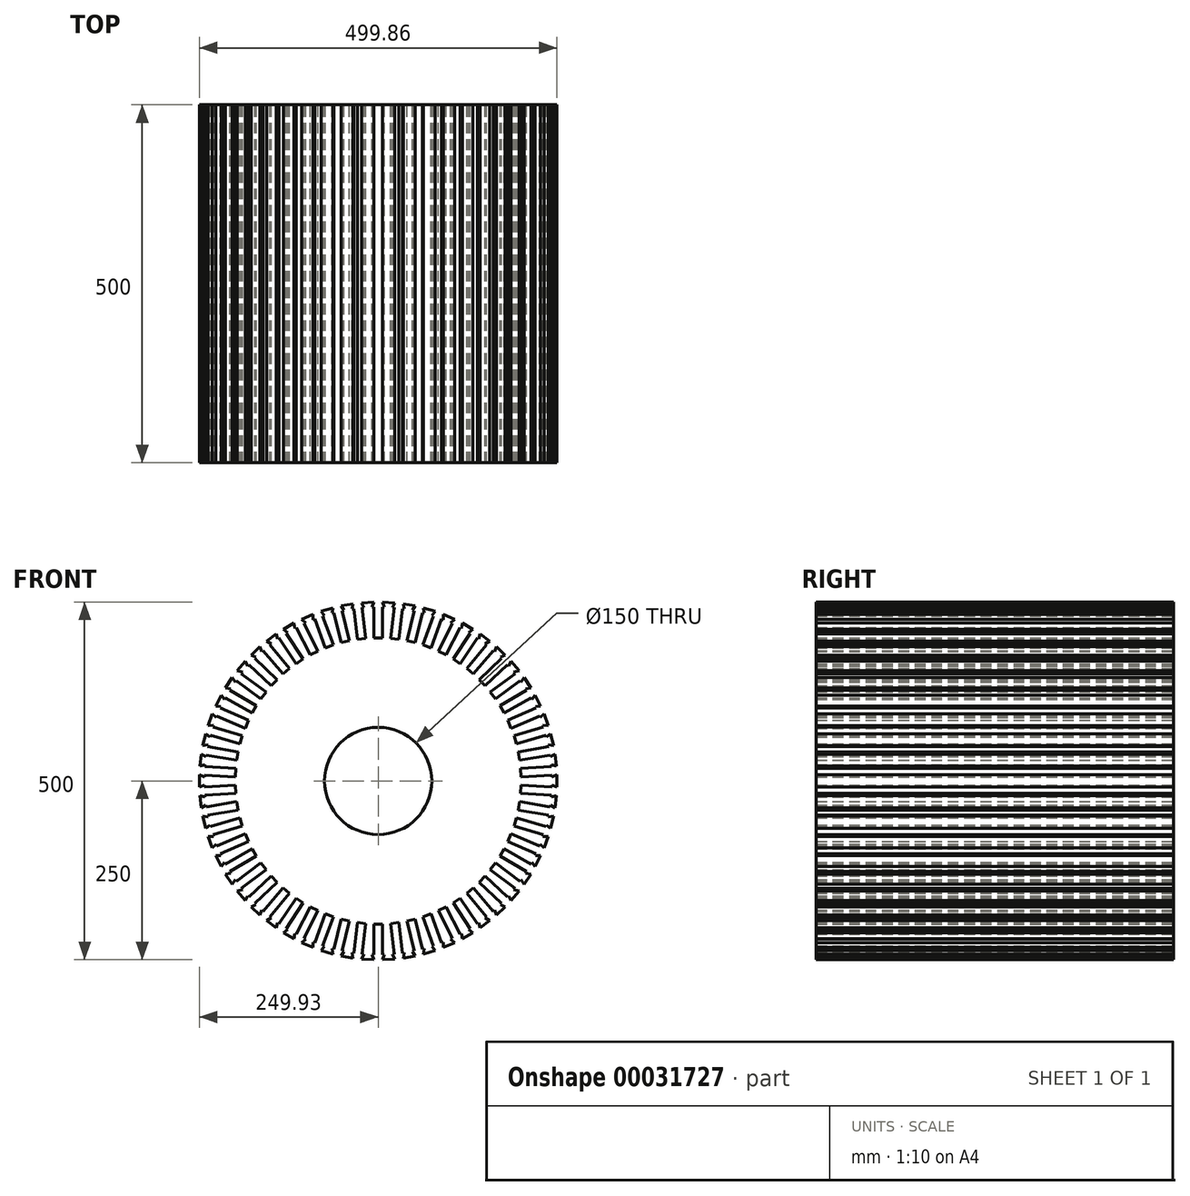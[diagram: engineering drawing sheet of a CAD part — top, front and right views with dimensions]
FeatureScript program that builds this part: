
annotation { "Feature Type Name" : "Feature", "Feature Type Description" : "" }
export const myFeature = defineFeature(function(context is Context, id is Id, definition is map)
    precondition{}
    {
        {
            var Q0;
            Q0=qCreatedBy(makeId("Front.planeOp"),FACE);
            var sketch = newSketch(context, id + "F0", { "sketchPlane" : qUnion([Q0])});
            skCircle(sketch, "E0", {"center": v(0, 0) * mm, "radius": 250 * mm, "construction": true});
            skCircle(sketch, "E1", {"center": v(0, 0) * mm, "radius": 75 * mm});
            skLineSegment(sketch, "E2", {"start": v(0, 0) * mm, "end": v(0, 250) * mm, "construction": true});
            skLineSegment(sketch, "E3.MirrorCS", {"start": v(6, 243) * mm, "end": v(6, 200) * mm});
            skPoint(sketch, "E4.orphan", {"position": v(6, 250) * mm});
            skLineSegment(sketch, "E5", {"start": v(-6, 243) * mm, "end": v(-6, 200) * mm});
            skLineSegment(sketch, "E6.MirrorCS", {"start": v(6, 200) * mm, "end": v(0, 200) * mm});
            skLineSegment(sketch, "E7", {"start": v(-6, 200) * mm, "end": v(0, 200) * mm});
            skLineSegment(sketch, "E8.MirrorCS", {"start": v(6, 250) * mm, "end": v(8.5, 243) * mm});
            skLineSegment(sketch, "E9.MirrorCS", {"start": v(6, 250) * mm, "end": v(0, 250) * mm, "construction": true});
            skLineSegment(sketch, "E10", {"start": v(-6, 250) * mm, "end": v(-8.5, 243) * mm});
            skLineSegment(sketch, "E11", {"start": v(-8.5, 243) * mm, "end": v(-6, 243) * mm});
            skLineSegment(sketch, "E12", {"start": v(0, 250) * mm, "end": v(0, -95.6) * mm, "construction": true});
            skLineSegment(sketch, "E13", {"start": v(-6, 250) * mm, "end": v(0, 250) * mm, "construction": true});
            skLineSegment(sketch, "E14.MirrorCS", {"start": v(8.5, 243) * mm, "end": v(6, 243) * mm});
            skLineSegment(sketch, "E15.1.0", {"start": v(-34.98, 247.61) * mm, "end": v(-29.02, 248.3) * mm, "construction": true});
            skLineSegment(sketch, "E15.1.1", {"start": v(-19.77, 242.34) * mm, "end": v(-22.25, 242.05) * mm});
            skLineSegment(sketch, "E15.1.4", {"start": v(-22.25, 242.05) * mm, "end": v(-17.26, 199.34) * mm});
            skLineSegment(sketch, "E15.1.5", {"start": v(-34.17, 240.66) * mm, "end": v(-29.18, 197.95) * mm});
            skLineSegment(sketch, "E15.1.6", {"start": v(-17.26, 199.34) * mm, "end": v(-23.22, 198.65) * mm});
            skLineSegment(sketch, "E15.1.9", {"start": v(-29.18, 197.95) * mm, "end": v(-23.22, 198.65) * mm});
            skPoint(sketch, "E15.1.15", {"position": v(-23.06, 249) * mm});
            skLineSegment(sketch, "E15.1.16", {"start": v(-34.98, 247.61) * mm, "end": v(-36.65, 240.37) * mm});
            skLineSegment(sketch, "E15.1.17", {"start": v(-23.06, 249) * mm, "end": v(-19.77, 242.34) * mm});
            skLineSegment(sketch, "E15.1.18", {"start": v(-23.06, 249) * mm, "end": v(-29.02, 248.3) * mm, "construction": true});
            skLineSegment(sketch, "E15.1.19", {"start": v(-36.65, 240.37) * mm, "end": v(-34.17, 240.66) * mm});
            skLineSegment(sketch, "E15.2.0", {"start": v(-63.5, 241.88) * mm, "end": v(-57.65, 243.26) * mm, "construction": true});
            skLineSegment(sketch, "E15.2.1", {"start": v(-47.77, 238.41) * mm, "end": v(-50.2, 237.83) * mm});
            skLineSegment(sketch, "E15.2.4", {"start": v(-50.2, 237.83) * mm, "end": v(-40.28, 196) * mm});
            skLineSegment(sketch, "E15.2.5", {"start": v(-61.88, 235.07) * mm, "end": v(-51.96, 193.23) * mm});
            skLineSegment(sketch, "E15.2.6", {"start": v(-40.28, 196) * mm, "end": v(-46.12, 194.6) * mm});
            skLineSegment(sketch, "E15.2.9", {"start": v(-51.96, 193.23) * mm, "end": v(-46.12, 194.6) * mm});
            skPoint(sketch, "E15.2.15", {"position": v(-51.82, 244.64) * mm});
            skLineSegment(sketch, "E15.2.16", {"start": v(-63.5, 241.88) * mm, "end": v(-64.31, 234.49) * mm});
            skLineSegment(sketch, "E15.2.17", {"start": v(-51.82, 244.64) * mm, "end": v(-47.77, 238.41) * mm});
            skLineSegment(sketch, "E15.2.18", {"start": v(-51.82, 244.64) * mm, "end": v(-57.65, 243.26) * mm, "construction": true});
            skLineSegment(sketch, "E15.2.19", {"start": v(-64.31, 234.49) * mm, "end": v(-61.88, 235.07) * mm});
            skLineSegment(sketch, "E15.3.0", {"start": v(-91.14, 232.87) * mm, "end": v(-85.5, 234.92) * mm, "construction": true});
            skLineSegment(sketch, "E15.3.1", {"start": v(-75.12, 231.25) * mm, "end": v(-77.47, 230.4) * mm});
            skLineSegment(sketch, "E15.3.4", {"start": v(-77.47, 230.4) * mm, "end": v(-62.77, 190) * mm});
            skLineSegment(sketch, "E15.3.5", {"start": v(-88.75, 226.3) * mm, "end": v(-74.04, 185.89) * mm});
            skLineSegment(sketch, "E15.3.6", {"start": v(-62.77, 190) * mm, "end": v(-68.4, 187.94) * mm});
            skLineSegment(sketch, "E15.3.9", {"start": v(-74.04, 185.89) * mm, "end": v(-68.4, 187.94) * mm});
            skPoint(sketch, "E15.3.15", {"position": v(-79.87, 236.98) * mm});
            skLineSegment(sketch, "E15.3.16", {"start": v(-91.14, 232.87) * mm, "end": v(-91.1, 225.44) * mm});
            skLineSegment(sketch, "E15.3.17", {"start": v(-79.87, 236.98) * mm, "end": v(-75.12, 231.25) * mm});
            skLineSegment(sketch, "E15.3.18", {"start": v(-79.87, 236.98) * mm, "end": v(-85.5, 234.92) * mm, "construction": true});
            skLineSegment(sketch, "E15.3.19", {"start": v(-91.1, 225.44) * mm, "end": v(-88.75, 226.3) * mm});
            skLineSegment(sketch, "E15.4.0", {"start": v(-117.56, 220.72) * mm, "end": v(-112.2, 223.4) * mm, "construction": true});
            skLineSegment(sketch, "E15.4.1", {"start": v(-101.46, 220.97) * mm, "end": v(-103.7, 219.85) * mm});
            skLineSegment(sketch, "E15.4.4", {"start": v(-103.7, 219.85) * mm, "end": v(-84.4, 181.42) * mm});
            skLineSegment(sketch, "E15.4.5", {"start": v(-114.42, 214.46) * mm, "end": v(-95.12, 176.03) * mm});
            skLineSegment(sketch, "E15.4.6", {"start": v(-84.4, 181.42) * mm, "end": v(-89.76, 178.73) * mm});
            skLineSegment(sketch, "E15.4.9", {"start": v(-95.12, 176.03) * mm, "end": v(-89.76, 178.73) * mm});
            skPoint(sketch, "E15.4.15", {"position": v(-106.84, 226.1) * mm});
            skLineSegment(sketch, "E15.4.16", {"start": v(-117.56, 220.72) * mm, "end": v(-116.65, 213.34) * mm});
            skLineSegment(sketch, "E15.4.17", {"start": v(-106.84, 226.1) * mm, "end": v(-101.46, 220.97) * mm});
            skLineSegment(sketch, "E15.4.18", {"start": v(-106.84, 226.1) * mm, "end": v(-112.2, 223.4) * mm, "construction": true});
            skLineSegment(sketch, "E15.4.19", {"start": v(-116.65, 213.34) * mm, "end": v(-114.42, 214.46) * mm});
            skLineSegment(sketch, "E15.5.0", {"start": v(-142.4, 205.57) * mm, "end": v(-137.38, 208.87) * mm, "construction": true});
            skLineSegment(sketch, "E15.5.1", {"start": v(-126.43, 207.7) * mm, "end": v(-128.52, 206.32) * mm});
            skLineSegment(sketch, "E15.5.4", {"start": v(-128.52, 206.32) * mm, "end": v(-104.89, 170.4) * mm});
            skLineSegment(sketch, "E15.5.5", {"start": v(-138.54, 199.73) * mm, "end": v(-114.91, 163.8) * mm});
            skLineSegment(sketch, "E15.5.6", {"start": v(-104.89, 170.4) * mm, "end": v(-109.9, 167.1) * mm});
            skLineSegment(sketch, "E15.5.9", {"start": v(-114.91, 163.8) * mm, "end": v(-109.9, 167.1) * mm});
            skPoint(sketch, "E15.5.15", {"position": v(-132.36, 212.17) * mm});
            skLineSegment(sketch, "E15.5.16", {"start": v(-142.4, 205.57) * mm, "end": v(-140.63, 198.35) * mm});
            skLineSegment(sketch, "E15.5.17", {"start": v(-132.36, 212.17) * mm, "end": v(-126.43, 207.7) * mm});
            skLineSegment(sketch, "E15.5.18", {"start": v(-132.36, 212.17) * mm, "end": v(-137.38, 208.87) * mm, "construction": true});
            skLineSegment(sketch, "E15.5.19", {"start": v(-140.63, 198.35) * mm, "end": v(-138.54, 199.73) * mm});
            skLineSegment(sketch, "E15.6.0", {"start": v(-165.3, 187.65) * mm, "end": v(-160.7, 191.51) * mm, "construction": true});
            skLineSegment(sketch, "E15.6.1", {"start": v(-149.69, 191.61) * mm, "end": v(-151.6, 190) * mm});
            skLineSegment(sketch, "E15.6.4", {"start": v(-151.6, 190) * mm, "end": v(-123.96, 157.07) * mm});
            skLineSegment(sketch, "E15.6.5", {"start": v(-160.8, 182.3) * mm, "end": v(-133.15, 149.35) * mm});
            skLineSegment(sketch, "E15.6.6", {"start": v(-123.96, 157.07) * mm, "end": v(-128.56, 153.2) * mm});
            skLineSegment(sketch, "E15.6.9", {"start": v(-133.15, 149.35) * mm, "end": v(-128.56, 153.2) * mm});
            skPoint(sketch, "E15.6.15", {"position": v(-156.1, 195.37) * mm});
            skLineSegment(sketch, "E15.6.16", {"start": v(-165.3, 187.65) * mm, "end": v(-162.7, 180.69) * mm});
            skLineSegment(sketch, "E15.6.17", {"start": v(-156.1, 195.37) * mm, "end": v(-149.69, 191.61) * mm});
            skLineSegment(sketch, "E15.6.18", {"start": v(-156.1, 195.37) * mm, "end": v(-160.7, 191.51) * mm, "construction": true});
            skLineSegment(sketch, "E15.6.19", {"start": v(-162.7, 180.69) * mm, "end": v(-160.8, 182.3) * mm});
            skLineSegment(sketch, "E15.7.0", {"start": v(-185.96, 167.2) * mm, "end": v(-181.84, 171.56) * mm, "construction": true});
            skLineSegment(sketch, "E15.7.1", {"start": v(-170.92, 172.94) * mm, "end": v(-172.63, 171.12) * mm});
            skLineSegment(sketch, "E15.7.4", {"start": v(-172.63, 171.12) * mm, "end": v(-141.36, 141.61) * mm});
            skLineSegment(sketch, "E15.7.5", {"start": v(-180.87, 162.4) * mm, "end": v(-149.6, 132.88) * mm});
            skLineSegment(sketch, "E15.7.6", {"start": v(-141.36, 141.61) * mm, "end": v(-145.47, 137.25) * mm});
            skLineSegment(sketch, "E15.7.9", {"start": v(-149.6, 132.88) * mm, "end": v(-145.47, 137.25) * mm});
            skPoint(sketch, "E15.7.15", {"position": v(-177.73, 175.92) * mm});
            skLineSegment(sketch, "E15.7.16", {"start": v(-185.96, 167.2) * mm, "end": v(-182.58, 160.57) * mm});
            skLineSegment(sketch, "E15.7.17", {"start": v(-177.73, 175.92) * mm, "end": v(-170.92, 172.94) * mm});
            skLineSegment(sketch, "E15.7.18", {"start": v(-177.73, 175.92) * mm, "end": v(-181.84, 171.56) * mm, "construction": true});
            skLineSegment(sketch, "E15.7.19", {"start": v(-182.58, 160.57) * mm, "end": v(-180.87, 162.4) * mm});
            skLineSegment(sketch, "E15.8.0", {"start": v(-204.11, 144.48) * mm, "end": v(-200.53, 149.29) * mm, "construction": true});
            skLineSegment(sketch, "E15.8.1", {"start": v(-189.84, 151.93) * mm, "end": v(-191.33, 149.92) * mm});
            skLineSegment(sketch, "E15.8.4", {"start": v(-191.33, 149.92) * mm, "end": v(-156.84, 124.24) * mm});
            skLineSegment(sketch, "E15.8.5", {"start": v(-198.5, 140.3) * mm, "end": v(-164, 114.62) * mm});
            skLineSegment(sketch, "E15.8.6", {"start": v(-156.84, 124.24) * mm, "end": v(-160.42, 119.43) * mm});
            skLineSegment(sketch, "E15.8.9", {"start": v(-164, 114.62) * mm, "end": v(-160.42, 119.43) * mm});
            skPoint(sketch, "E15.8.15", {"position": v(-196.95, 154.1) * mm});
            skLineSegment(sketch, "E15.8.16", {"start": v(-204.11, 144.48) * mm, "end": v(-200, 138.3) * mm});
            skLineSegment(sketch, "E15.8.17", {"start": v(-196.95, 154.1) * mm, "end": v(-189.84, 151.93) * mm});
            skLineSegment(sketch, "E15.8.18", {"start": v(-196.95, 154.1) * mm, "end": v(-200.53, 149.29) * mm, "construction": true});
            skLineSegment(sketch, "E15.8.19", {"start": v(-200, 138.3) * mm, "end": v(-198.5, 140.3) * mm});
            skLineSegment(sketch, "E15.9.0", {"start": v(-219.5, 119.8) * mm, "end": v(-216.5, 125) * mm, "construction": true});
            skLineSegment(sketch, "E15.9.1", {"start": v(-206.2, 128.86) * mm, "end": v(-207.44, 126.7) * mm});
            skLineSegment(sketch, "E15.9.4", {"start": v(-207.44, 126.7) * mm, "end": v(-170.2, 105.2) * mm});
            skLineSegment(sketch, "E15.9.5", {"start": v(-213.44, 116.3) * mm, "end": v(-176.2, 94.8) * mm});
            skLineSegment(sketch, "E15.9.6", {"start": v(-170.2, 105.2) * mm, "end": v(-173.2, 100) * mm});
            skLineSegment(sketch, "E15.9.9", {"start": v(-176.2, 94.8) * mm, "end": v(-173.2, 100) * mm});
            skPoint(sketch, "E15.9.15", {"position": v(-213.5, 130.2) * mm});
            skLineSegment(sketch, "E15.9.16", {"start": v(-219.5, 119.8) * mm, "end": v(-214.7, 114.14) * mm});
            skLineSegment(sketch, "E15.9.17", {"start": v(-213.5, 130.2) * mm, "end": v(-206.2, 128.86) * mm});
            skLineSegment(sketch, "E15.9.18", {"start": v(-213.5, 130.2) * mm, "end": v(-216.5, 125) * mm, "construction": true});
            skLineSegment(sketch, "E15.9.19", {"start": v(-214.7, 114.14) * mm, "end": v(-213.44, 116.3) * mm});
            skLineSegment(sketch, "E15.10.0", {"start": v(-231.93, 93.51) * mm, "end": v(-229.55, 99.02) * mm, "construction": true});
            skLineSegment(sketch, "E15.10.1", {"start": v(-219.76, 104.05) * mm, "end": v(-220.75, 101.76) * mm});
            skLineSegment(sketch, "E15.10.4", {"start": v(-220.75, 101.76) * mm, "end": v(-181.27, 84.73) * mm});
            skLineSegment(sketch, "E15.10.5", {"start": v(-225.5, 90.74) * mm, "end": v(-186.02, 73.7) * mm});
            skLineSegment(sketch, "E15.10.6", {"start": v(-181.27, 84.73) * mm, "end": v(-183.64, 79.22) * mm});
            skLineSegment(sketch, "E15.10.9", {"start": v(-186.02, 73.7) * mm, "end": v(-183.64, 79.22) * mm});
            skPoint(sketch, "E15.10.15", {"position": v(-227.18, 104.53) * mm});
            skLineSegment(sketch, "E15.10.16", {"start": v(-231.93, 93.51) * mm, "end": v(-226.5, 88.44) * mm});
            skLineSegment(sketch, "E15.10.17", {"start": v(-227.18, 104.53) * mm, "end": v(-219.76, 104.05) * mm});
            skLineSegment(sketch, "E15.10.18", {"start": v(-227.18, 104.53) * mm, "end": v(-229.55, 99.02) * mm, "construction": true});
            skLineSegment(sketch, "E15.10.19", {"start": v(-226.5, 88.44) * mm, "end": v(-225.5, 90.74) * mm});
            skLineSegment(sketch, "E15.11.0", {"start": v(-241.22, 65.95) * mm, "end": v(-239.5, 71.7) * mm, "construction": true});
            skLineSegment(sketch, "E15.11.1", {"start": v(-230.35, 77.84) * mm, "end": v(-231.07, 75.44) * mm});
            skLineSegment(sketch, "E15.11.4", {"start": v(-231.07, 75.44) * mm, "end": v(-189.88, 63.1) * mm});
            skLineSegment(sketch, "E15.11.5", {"start": v(-234.51, 63.95) * mm, "end": v(-193.32, 51.61) * mm});
            skLineSegment(sketch, "E15.11.6", {"start": v(-189.88, 63.1) * mm, "end": v(-191.6, 57.36) * mm});
            skLineSegment(sketch, "E15.11.9", {"start": v(-193.32, 51.61) * mm, "end": v(-191.6, 57.36) * mm});
            skPoint(sketch, "E15.11.15", {"position": v(-237.78, 77.45) * mm});
            skLineSegment(sketch, "E15.11.16", {"start": v(-241.22, 65.95) * mm, "end": v(-235.23, 61.55) * mm});
            skLineSegment(sketch, "E15.11.17", {"start": v(-237.78, 77.45) * mm, "end": v(-230.35, 77.84) * mm});
            skLineSegment(sketch, "E15.11.18", {"start": v(-237.78, 77.45) * mm, "end": v(-239.5, 71.7) * mm, "construction": true});
            skLineSegment(sketch, "E15.11.19", {"start": v(-235.23, 61.55) * mm, "end": v(-234.51, 63.95) * mm});
            skLineSegment(sketch, "E15.12.0", {"start": v(-247.24, 37.5) * mm, "end": v(-246.2, 43.41) * mm, "construction": true});
            skLineSegment(sketch, "E15.12.1", {"start": v(-237.83, 50.57) * mm, "end": v(-238.27, 48.1) * mm});
            skLineSegment(sketch, "E15.12.4", {"start": v(-238.27, 48.1) * mm, "end": v(-195.92, 40.64) * mm});
            skLineSegment(sketch, "E15.12.5", {"start": v(-240.35, 36.29) * mm, "end": v(-198, 28.82) * mm});
            skLineSegment(sketch, "E15.12.6", {"start": v(-195.92, 40.64) * mm, "end": v(-196.96, 34.73) * mm});
            skLineSegment(sketch, "E15.12.9", {"start": v(-198, 28.82) * mm, "end": v(-196.96, 34.73) * mm});
            skPoint(sketch, "E15.12.15", {"position": v(-245.16, 49.32) * mm});
            skLineSegment(sketch, "E15.12.16", {"start": v(-247.24, 37.5) * mm, "end": v(-240.78, 33.83) * mm});
            skLineSegment(sketch, "E15.12.17", {"start": v(-245.16, 49.32) * mm, "end": v(-237.83, 50.57) * mm});
            skLineSegment(sketch, "E15.12.18", {"start": v(-245.16, 49.32) * mm, "end": v(-246.2, 43.41) * mm, "construction": true});
            skLineSegment(sketch, "E15.12.19", {"start": v(-240.78, 33.83) * mm, "end": v(-240.35, 36.29) * mm});
            skLineSegment(sketch, "E15.13.0", {"start": v(-249.93, 8.55) * mm, "end": v(-249.58, 14.54) * mm, "construction": true});
            skLineSegment(sketch, "E15.13.1", {"start": v(-242.1, 22.61) * mm, "end": v(-242.24, 20.12) * mm});
            skLineSegment(sketch, "E15.13.4", {"start": v(-242.24, 20.12) * mm, "end": v(-199.31, 17.62) * mm});
            skLineSegment(sketch, "E15.13.5", {"start": v(-242.94, 8.14) * mm, "end": v(-200.01, 5.64) * mm});
            skLineSegment(sketch, "E15.13.6", {"start": v(-199.31, 17.62) * mm, "end": v(-199.66, 11.63) * mm});
            skLineSegment(sketch, "E15.13.9", {"start": v(-200.01, 5.64) * mm, "end": v(-199.66, 11.63) * mm});
            skPoint(sketch, "E15.13.15", {"position": v(-249.23, 20.53) * mm});
            skLineSegment(sketch, "E15.13.16", {"start": v(-249.93, 8.55) * mm, "end": v(-243.08, 5.64) * mm});
            skLineSegment(sketch, "E15.13.17", {"start": v(-249.23, 20.53) * mm, "end": v(-242.1, 22.61) * mm});
            skLineSegment(sketch, "E15.13.18", {"start": v(-249.23, 20.53) * mm, "end": v(-249.58, 14.54) * mm, "construction": true});
            skLineSegment(sketch, "E15.13.19", {"start": v(-243.08, 5.64) * mm, "end": v(-242.94, 8.14) * mm});
            skLineSegment(sketch, "E15.14.0", {"start": v(-249.23, -20.53) * mm, "end": v(-249.58, -14.54) * mm, "construction": true});
            skLineSegment(sketch, "E15.14.1", {"start": v(-243.08, -5.64) * mm, "end": v(-242.94, -8.14) * mm});
            skLineSegment(sketch, "E15.14.4", {"start": v(-242.94, -8.14) * mm, "end": v(-200.01, -5.64) * mm});
            skLineSegment(sketch, "E15.14.5", {"start": v(-242.24, -20.12) * mm, "end": v(-199.31, -17.62) * mm});
            skLineSegment(sketch, "E15.14.6", {"start": v(-200.01, -5.64) * mm, "end": v(-199.66, -11.63) * mm});
            skLineSegment(sketch, "E15.14.9", {"start": v(-199.31, -17.62) * mm, "end": v(-199.66, -11.63) * mm});
            skPoint(sketch, "E15.14.15", {"position": v(-249.93, -8.55) * mm});
            skLineSegment(sketch, "E15.14.16", {"start": v(-249.23, -20.53) * mm, "end": v(-242.1, -22.61) * mm});
            skLineSegment(sketch, "E15.14.17", {"start": v(-249.93, -8.55) * mm, "end": v(-243.08, -5.64) * mm});
            skLineSegment(sketch, "E15.14.18", {"start": v(-249.93, -8.55) * mm, "end": v(-249.58, -14.54) * mm, "construction": true});
            skLineSegment(sketch, "E15.14.19", {"start": v(-242.1, -22.61) * mm, "end": v(-242.24, -20.12) * mm});
            skLineSegment(sketch, "E15.15.0", {"start": v(-245.16, -49.32) * mm, "end": v(-246.2, -43.41) * mm, "construction": true});
            skLineSegment(sketch, "E15.15.1", {"start": v(-240.78, -33.83) * mm, "end": v(-240.35, -36.29) * mm});
            skLineSegment(sketch, "E15.15.4", {"start": v(-240.35, -36.29) * mm, "end": v(-198, -28.82) * mm});
            skLineSegment(sketch, "E15.15.5", {"start": v(-238.27, -48.1) * mm, "end": v(-195.92, -40.64) * mm});
            skLineSegment(sketch, "E15.15.6", {"start": v(-198, -28.82) * mm, "end": v(-196.96, -34.73) * mm});
            skLineSegment(sketch, "E15.15.9", {"start": v(-195.92, -40.64) * mm, "end": v(-196.96, -34.73) * mm});
            skPoint(sketch, "E15.15.15", {"position": v(-247.24, -37.5) * mm});
            skLineSegment(sketch, "E15.15.16", {"start": v(-245.16, -49.32) * mm, "end": v(-237.83, -50.57) * mm});
            skLineSegment(sketch, "E15.15.17", {"start": v(-247.24, -37.5) * mm, "end": v(-240.78, -33.83) * mm});
            skLineSegment(sketch, "E15.15.18", {"start": v(-247.24, -37.5) * mm, "end": v(-246.2, -43.41) * mm, "construction": true});
            skLineSegment(sketch, "E15.15.19", {"start": v(-237.83, -50.57) * mm, "end": v(-238.27, -48.1) * mm});
            skLineSegment(sketch, "E15.16.0", {"start": v(-237.78, -77.45) * mm, "end": v(-239.5, -71.7) * mm, "construction": true});
            skLineSegment(sketch, "E15.16.1", {"start": v(-235.23, -61.55) * mm, "end": v(-234.51, -63.95) * mm});
            skLineSegment(sketch, "E15.16.4", {"start": v(-234.51, -63.95) * mm, "end": v(-193.32, -51.61) * mm});
            skLineSegment(sketch, "E15.16.5", {"start": v(-231.07, -75.44) * mm, "end": v(-189.88, -63.1) * mm});
            skLineSegment(sketch, "E15.16.6", {"start": v(-193.32, -51.61) * mm, "end": v(-191.6, -57.36) * mm});
            skLineSegment(sketch, "E15.16.9", {"start": v(-189.88, -63.1) * mm, "end": v(-191.6, -57.36) * mm});
            skPoint(sketch, "E15.16.15", {"position": v(-241.22, -65.95) * mm});
            skLineSegment(sketch, "E15.16.16", {"start": v(-237.78, -77.45) * mm, "end": v(-230.35, -77.84) * mm});
            skLineSegment(sketch, "E15.16.17", {"start": v(-241.22, -65.95) * mm, "end": v(-235.23, -61.55) * mm});
            skLineSegment(sketch, "E15.16.18", {"start": v(-241.22, -65.95) * mm, "end": v(-239.5, -71.7) * mm, "construction": true});
            skLineSegment(sketch, "E15.16.19", {"start": v(-230.35, -77.84) * mm, "end": v(-231.07, -75.44) * mm});
            skLineSegment(sketch, "E15.17.0", {"start": v(-227.18, -104.53) * mm, "end": v(-229.55, -99.02) * mm, "construction": true});
            skLineSegment(sketch, "E15.17.1", {"start": v(-226.5, -88.44) * mm, "end": v(-225.5, -90.74) * mm});
            skLineSegment(sketch, "E15.17.4", {"start": v(-225.5, -90.74) * mm, "end": v(-186.02, -73.7) * mm});
            skLineSegment(sketch, "E15.17.5", {"start": v(-220.75, -101.76) * mm, "end": v(-181.27, -84.73) * mm});
            skLineSegment(sketch, "E15.17.6", {"start": v(-186.02, -73.7) * mm, "end": v(-183.64, -79.22) * mm});
            skLineSegment(sketch, "E15.17.9", {"start": v(-181.27, -84.73) * mm, "end": v(-183.64, -79.22) * mm});
            skPoint(sketch, "E15.17.15", {"position": v(-231.93, -93.51) * mm});
            skLineSegment(sketch, "E15.17.16", {"start": v(-227.18, -104.53) * mm, "end": v(-219.76, -104.05) * mm});
            skLineSegment(sketch, "E15.17.17", {"start": v(-231.93, -93.51) * mm, "end": v(-226.5, -88.44) * mm});
            skLineSegment(sketch, "E15.17.18", {"start": v(-231.93, -93.51) * mm, "end": v(-229.55, -99.02) * mm, "construction": true});
            skLineSegment(sketch, "E15.17.19", {"start": v(-219.76, -104.05) * mm, "end": v(-220.75, -101.76) * mm});
            skLineSegment(sketch, "E15.18.0", {"start": v(-213.5, -130.2) * mm, "end": v(-216.5, -125) * mm, "construction": true});
            skLineSegment(sketch, "E15.18.1", {"start": v(-214.7, -114.14) * mm, "end": v(-213.44, -116.3) * mm});
            skLineSegment(sketch, "E15.18.4", {"start": v(-213.44, -116.3) * mm, "end": v(-176.2, -94.8) * mm});
            skLineSegment(sketch, "E15.18.5", {"start": v(-207.44, -126.7) * mm, "end": v(-170.2, -105.2) * mm});
            skLineSegment(sketch, "E15.18.6", {"start": v(-176.2, -94.8) * mm, "end": v(-173.2, -100) * mm});
            skLineSegment(sketch, "E15.18.9", {"start": v(-170.2, -105.2) * mm, "end": v(-173.2, -100) * mm});
            skPoint(sketch, "E15.18.15", {"position": v(-219.5, -119.8) * mm});
            skLineSegment(sketch, "E15.18.16", {"start": v(-213.5, -130.2) * mm, "end": v(-206.2, -128.86) * mm});
            skLineSegment(sketch, "E15.18.17", {"start": v(-219.5, -119.8) * mm, "end": v(-214.7, -114.14) * mm});
            skLineSegment(sketch, "E15.18.18", {"start": v(-219.5, -119.8) * mm, "end": v(-216.5, -125) * mm, "construction": true});
            skLineSegment(sketch, "E15.18.19", {"start": v(-206.2, -128.86) * mm, "end": v(-207.44, -126.7) * mm});
            skLineSegment(sketch, "E15.19.0", {"start": v(-196.95, -154.1) * mm, "end": v(-200.53, -149.29) * mm, "construction": true});
            skLineSegment(sketch, "E15.19.1", {"start": v(-200, -138.3) * mm, "end": v(-198.5, -140.3) * mm});
            skLineSegment(sketch, "E15.19.4", {"start": v(-198.5, -140.3) * mm, "end": v(-164, -114.62) * mm});
            skLineSegment(sketch, "E15.19.5", {"start": v(-191.33, -149.92) * mm, "end": v(-156.84, -124.24) * mm});
            skLineSegment(sketch, "E15.19.6", {"start": v(-164, -114.62) * mm, "end": v(-160.42, -119.43) * mm});
            skLineSegment(sketch, "E15.19.9", {"start": v(-156.84, -124.24) * mm, "end": v(-160.42, -119.43) * mm});
            skPoint(sketch, "E15.19.15", {"position": v(-204.11, -144.48) * mm});
            skLineSegment(sketch, "E15.19.16", {"start": v(-196.95, -154.1) * mm, "end": v(-189.84, -151.93) * mm});
            skLineSegment(sketch, "E15.19.17", {"start": v(-204.11, -144.48) * mm, "end": v(-200, -138.3) * mm});
            skLineSegment(sketch, "E15.19.18", {"start": v(-204.11, -144.48) * mm, "end": v(-200.53, -149.29) * mm, "construction": true});
            skLineSegment(sketch, "E15.19.19", {"start": v(-189.84, -151.93) * mm, "end": v(-191.33, -149.92) * mm});
            skLineSegment(sketch, "E15.20.0", {"start": v(-177.73, -175.92) * mm, "end": v(-181.84, -171.56) * mm, "construction": true});
            skLineSegment(sketch, "E15.20.1", {"start": v(-182.58, -160.57) * mm, "end": v(-180.87, -162.4) * mm});
            skLineSegment(sketch, "E15.20.4", {"start": v(-180.87, -162.4) * mm, "end": v(-149.6, -132.88) * mm});
            skLineSegment(sketch, "E15.20.5", {"start": v(-172.63, -171.12) * mm, "end": v(-141.36, -141.61) * mm});
            skLineSegment(sketch, "E15.20.6", {"start": v(-149.6, -132.88) * mm, "end": v(-145.47, -137.25) * mm});
            skLineSegment(sketch, "E15.20.9", {"start": v(-141.36, -141.61) * mm, "end": v(-145.47, -137.25) * mm});
            skPoint(sketch, "E15.20.15", {"position": v(-185.96, -167.2) * mm});
            skLineSegment(sketch, "E15.20.16", {"start": v(-177.73, -175.92) * mm, "end": v(-170.92, -172.94) * mm});
            skLineSegment(sketch, "E15.20.17", {"start": v(-185.96, -167.2) * mm, "end": v(-182.58, -160.57) * mm});
            skLineSegment(sketch, "E15.20.18", {"start": v(-185.96, -167.2) * mm, "end": v(-181.84, -171.56) * mm, "construction": true});
            skLineSegment(sketch, "E15.20.19", {"start": v(-170.92, -172.94) * mm, "end": v(-172.63, -171.12) * mm});
            skLineSegment(sketch, "E15.21.0", {"start": v(-156.1, -195.37) * mm, "end": v(-160.7, -191.51) * mm, "construction": true});
            skLineSegment(sketch, "E15.21.1", {"start": v(-162.7, -180.69) * mm, "end": v(-160.8, -182.3) * mm});
            skLineSegment(sketch, "E15.21.4", {"start": v(-160.8, -182.3) * mm, "end": v(-133.15, -149.35) * mm});
            skLineSegment(sketch, "E15.21.5", {"start": v(-151.6, -190) * mm, "end": v(-123.96, -157.07) * mm});
            skLineSegment(sketch, "E15.21.6", {"start": v(-133.15, -149.35) * mm, "end": v(-128.56, -153.2) * mm});
            skLineSegment(sketch, "E15.21.9", {"start": v(-123.96, -157.07) * mm, "end": v(-128.56, -153.2) * mm});
            skPoint(sketch, "E15.21.15", {"position": v(-165.3, -187.65) * mm});
            skLineSegment(sketch, "E15.21.16", {"start": v(-156.1, -195.37) * mm, "end": v(-149.69, -191.61) * mm});
            skLineSegment(sketch, "E15.21.17", {"start": v(-165.3, -187.65) * mm, "end": v(-162.7, -180.69) * mm});
            skLineSegment(sketch, "E15.21.18", {"start": v(-165.3, -187.65) * mm, "end": v(-160.7, -191.51) * mm, "construction": true});
            skLineSegment(sketch, "E15.21.19", {"start": v(-149.69, -191.61) * mm, "end": v(-151.6, -190) * mm});
            skLineSegment(sketch, "E15.22.0", {"start": v(-132.36, -212.17) * mm, "end": v(-137.38, -208.87) * mm, "construction": true});
            skLineSegment(sketch, "E15.22.1", {"start": v(-140.63, -198.35) * mm, "end": v(-138.54, -199.73) * mm});
            skLineSegment(sketch, "E15.22.4", {"start": v(-138.54, -199.73) * mm, "end": v(-114.91, -163.8) * mm});
            skLineSegment(sketch, "E15.22.5", {"start": v(-128.52, -206.32) * mm, "end": v(-104.89, -170.4) * mm});
            skLineSegment(sketch, "E15.22.6", {"start": v(-114.91, -163.8) * mm, "end": v(-109.9, -167.1) * mm});
            skLineSegment(sketch, "E15.22.9", {"start": v(-104.89, -170.4) * mm, "end": v(-109.9, -167.1) * mm});
            skPoint(sketch, "E15.22.15", {"position": v(-142.4, -205.57) * mm});
            skLineSegment(sketch, "E15.22.16", {"start": v(-132.36, -212.17) * mm, "end": v(-126.43, -207.7) * mm});
            skLineSegment(sketch, "E15.22.17", {"start": v(-142.4, -205.57) * mm, "end": v(-140.63, -198.35) * mm});
            skLineSegment(sketch, "E15.22.18", {"start": v(-142.4, -205.57) * mm, "end": v(-137.38, -208.87) * mm, "construction": true});
            skLineSegment(sketch, "E15.22.19", {"start": v(-126.43, -207.7) * mm, "end": v(-128.52, -206.32) * mm});
            skLineSegment(sketch, "E15.23.0", {"start": v(-106.84, -226.1) * mm, "end": v(-112.2, -223.4) * mm, "construction": true});
            skLineSegment(sketch, "E15.23.1", {"start": v(-116.65, -213.34) * mm, "end": v(-114.42, -214.46) * mm});
            skLineSegment(sketch, "E15.23.4", {"start": v(-114.42, -214.46) * mm, "end": v(-95.12, -176.03) * mm});
            skLineSegment(sketch, "E15.23.5", {"start": v(-103.7, -219.85) * mm, "end": v(-84.4, -181.42) * mm});
            skLineSegment(sketch, "E15.23.6", {"start": v(-95.12, -176.03) * mm, "end": v(-89.76, -178.73) * mm});
            skLineSegment(sketch, "E15.23.9", {"start": v(-84.4, -181.42) * mm, "end": v(-89.76, -178.73) * mm});
            skPoint(sketch, "E15.23.15", {"position": v(-117.56, -220.72) * mm});
            skLineSegment(sketch, "E15.23.16", {"start": v(-106.84, -226.1) * mm, "end": v(-101.46, -220.97) * mm});
            skLineSegment(sketch, "E15.23.17", {"start": v(-117.56, -220.72) * mm, "end": v(-116.65, -213.34) * mm});
            skLineSegment(sketch, "E15.23.18", {"start": v(-117.56, -220.72) * mm, "end": v(-112.2, -223.4) * mm, "construction": true});
            skLineSegment(sketch, "E15.23.19", {"start": v(-101.46, -220.97) * mm, "end": v(-103.7, -219.85) * mm});
            skLineSegment(sketch, "E15.24.0", {"start": v(-79.87, -236.98) * mm, "end": v(-85.5, -234.92) * mm, "construction": true});
            skLineSegment(sketch, "E15.24.1", {"start": v(-91.1, -225.44) * mm, "end": v(-88.75, -226.3) * mm});
            skLineSegment(sketch, "E15.24.4", {"start": v(-88.75, -226.3) * mm, "end": v(-74.04, -185.89) * mm});
            skLineSegment(sketch, "E15.24.5", {"start": v(-77.47, -230.4) * mm, "end": v(-62.77, -190) * mm});
            skLineSegment(sketch, "E15.24.6", {"start": v(-74.04, -185.89) * mm, "end": v(-68.4, -187.94) * mm});
            skLineSegment(sketch, "E15.24.9", {"start": v(-62.77, -190) * mm, "end": v(-68.4, -187.94) * mm});
            skPoint(sketch, "E15.24.15", {"position": v(-91.14, -232.87) * mm});
            skLineSegment(sketch, "E15.24.16", {"start": v(-79.87, -236.98) * mm, "end": v(-75.12, -231.25) * mm});
            skLineSegment(sketch, "E15.24.17", {"start": v(-91.14, -232.87) * mm, "end": v(-91.1, -225.44) * mm});
            skLineSegment(sketch, "E15.24.18", {"start": v(-91.14, -232.87) * mm, "end": v(-85.5, -234.92) * mm, "construction": true});
            skLineSegment(sketch, "E15.24.19", {"start": v(-75.12, -231.25) * mm, "end": v(-77.47, -230.4) * mm});
            skLineSegment(sketch, "E15.25.0", {"start": v(-51.82, -244.64) * mm, "end": v(-57.65, -243.26) * mm, "construction": true});
            skLineSegment(sketch, "E15.25.1", {"start": v(-64.31, -234.49) * mm, "end": v(-61.88, -235.07) * mm});
            skLineSegment(sketch, "E15.25.4", {"start": v(-61.88, -235.07) * mm, "end": v(-51.96, -193.23) * mm});
            skLineSegment(sketch, "E15.25.5", {"start": v(-50.2, -237.83) * mm, "end": v(-40.28, -196) * mm});
            skLineSegment(sketch, "E15.25.6", {"start": v(-51.96, -193.23) * mm, "end": v(-46.12, -194.6) * mm});
            skLineSegment(sketch, "E15.25.9", {"start": v(-40.28, -196) * mm, "end": v(-46.12, -194.6) * mm});
            skPoint(sketch, "E15.25.15", {"position": v(-63.5, -241.88) * mm});
            skLineSegment(sketch, "E15.25.16", {"start": v(-51.82, -244.64) * mm, "end": v(-47.77, -238.41) * mm});
            skLineSegment(sketch, "E15.25.17", {"start": v(-63.5, -241.88) * mm, "end": v(-64.31, -234.49) * mm});
            skLineSegment(sketch, "E15.25.18", {"start": v(-63.5, -241.88) * mm, "end": v(-57.65, -243.26) * mm, "construction": true});
            skLineSegment(sketch, "E15.25.19", {"start": v(-47.77, -238.41) * mm, "end": v(-50.2, -237.83) * mm});
            skLineSegment(sketch, "E15.26.0", {"start": v(-23.06, -249) * mm, "end": v(-29.02, -248.3) * mm, "construction": true});
            skLineSegment(sketch, "E15.26.1", {"start": v(-36.65, -240.37) * mm, "end": v(-34.17, -240.66) * mm});
            skLineSegment(sketch, "E15.26.4", {"start": v(-34.17, -240.66) * mm, "end": v(-29.18, -197.95) * mm});
            skLineSegment(sketch, "E15.26.5", {"start": v(-22.25, -242.05) * mm, "end": v(-17.26, -199.34) * mm});
            skLineSegment(sketch, "E15.26.6", {"start": v(-29.18, -197.95) * mm, "end": v(-23.22, -198.65) * mm});
            skLineSegment(sketch, "E15.26.9", {"start": v(-17.26, -199.34) * mm, "end": v(-23.22, -198.65) * mm});
            skPoint(sketch, "E15.26.15", {"position": v(-34.98, -247.61) * mm});
            skLineSegment(sketch, "E15.26.16", {"start": v(-23.06, -249) * mm, "end": v(-19.77, -242.34) * mm});
            skLineSegment(sketch, "E15.26.17", {"start": v(-34.98, -247.61) * mm, "end": v(-36.65, -240.37) * mm});
            skLineSegment(sketch, "E15.26.18", {"start": v(-34.98, -247.61) * mm, "end": v(-29.02, -248.3) * mm, "construction": true});
            skLineSegment(sketch, "E15.26.19", {"start": v(-19.77, -242.34) * mm, "end": v(-22.25, -242.05) * mm});
            skLineSegment(sketch, "E15.27.0", {"start": v(6, -250) * mm, "end": v(0, -250) * mm, "construction": true});
            skLineSegment(sketch, "E15.27.1", {"start": v(-8.5, -243) * mm, "end": v(-6, -243) * mm});
            skLineSegment(sketch, "E15.27.4", {"start": v(-6, -243) * mm, "end": v(-6, -200) * mm});
            skLineSegment(sketch, "E15.27.5", {"start": v(6, -243) * mm, "end": v(6, -200) * mm});
            skLineSegment(sketch, "E15.27.6", {"start": v(-6, -200) * mm, "end": v(0, -200) * mm});
            skLineSegment(sketch, "E15.27.9", {"start": v(6, -200) * mm, "end": v(0, -200) * mm});
            skPoint(sketch, "E15.27.15", {"position": v(-6, -250) * mm});
            skLineSegment(sketch, "E15.27.16", {"start": v(6, -250) * mm, "end": v(8.5, -243) * mm});
            skLineSegment(sketch, "E15.27.17", {"start": v(-6, -250) * mm, "end": v(-8.5, -243) * mm});
            skLineSegment(sketch, "E15.27.18", {"start": v(-6, -250) * mm, "end": v(0, -250) * mm, "construction": true});
            skLineSegment(sketch, "E15.27.19", {"start": v(8.5, -243) * mm, "end": v(6, -243) * mm});
            skLineSegment(sketch, "E15.28.0", {"start": v(34.98, -247.61) * mm, "end": v(29.02, -248.3) * mm, "construction": true});
            skLineSegment(sketch, "E15.28.1", {"start": v(19.77, -242.34) * mm, "end": v(22.25, -242.05) * mm});
            skLineSegment(sketch, "E15.28.4", {"start": v(22.25, -242.05) * mm, "end": v(17.26, -199.34) * mm});
            skLineSegment(sketch, "E15.28.5", {"start": v(34.17, -240.66) * mm, "end": v(29.18, -197.95) * mm});
            skLineSegment(sketch, "E15.28.6", {"start": v(17.26, -199.34) * mm, "end": v(23.22, -198.65) * mm});
            skLineSegment(sketch, "E15.28.9", {"start": v(29.18, -197.95) * mm, "end": v(23.22, -198.65) * mm});
            skPoint(sketch, "E15.28.15", {"position": v(23.06, -249) * mm});
            skLineSegment(sketch, "E15.28.16", {"start": v(34.98, -247.61) * mm, "end": v(36.65, -240.37) * mm});
            skLineSegment(sketch, "E15.28.17", {"start": v(23.06, -249) * mm, "end": v(19.77, -242.34) * mm});
            skLineSegment(sketch, "E15.28.18", {"start": v(23.06, -249) * mm, "end": v(29.02, -248.3) * mm, "construction": true});
            skLineSegment(sketch, "E15.28.19", {"start": v(36.65, -240.37) * mm, "end": v(34.17, -240.66) * mm});
            skLineSegment(sketch, "E15.29.0", {"start": v(63.5, -241.88) * mm, "end": v(57.65, -243.26) * mm, "construction": true});
            skLineSegment(sketch, "E15.29.1", {"start": v(47.77, -238.41) * mm, "end": v(50.2, -237.83) * mm});
            skLineSegment(sketch, "E15.29.4", {"start": v(50.2, -237.83) * mm, "end": v(40.28, -196) * mm});
            skLineSegment(sketch, "E15.29.5", {"start": v(61.88, -235.07) * mm, "end": v(51.96, -193.23) * mm});
            skLineSegment(sketch, "E15.29.6", {"start": v(40.28, -196) * mm, "end": v(46.12, -194.6) * mm});
            skLineSegment(sketch, "E15.29.9", {"start": v(51.96, -193.23) * mm, "end": v(46.12, -194.6) * mm});
            skPoint(sketch, "E15.29.15", {"position": v(51.82, -244.64) * mm});
            skLineSegment(sketch, "E15.29.16", {"start": v(63.5, -241.88) * mm, "end": v(64.31, -234.49) * mm});
            skLineSegment(sketch, "E15.29.17", {"start": v(51.82, -244.64) * mm, "end": v(47.77, -238.41) * mm});
            skLineSegment(sketch, "E15.29.18", {"start": v(51.82, -244.64) * mm, "end": v(57.65, -243.26) * mm, "construction": true});
            skLineSegment(sketch, "E15.29.19", {"start": v(64.31, -234.49) * mm, "end": v(61.88, -235.07) * mm});
            skLineSegment(sketch, "E15.30.0", {"start": v(91.14, -232.87) * mm, "end": v(85.5, -234.92) * mm, "construction": true});
            skLineSegment(sketch, "E15.30.1", {"start": v(75.12, -231.25) * mm, "end": v(77.47, -230.4) * mm});
            skLineSegment(sketch, "E15.30.4", {"start": v(77.47, -230.4) * mm, "end": v(62.77, -190) * mm});
            skLineSegment(sketch, "E15.30.5", {"start": v(88.75, -226.3) * mm, "end": v(74.04, -185.89) * mm});
            skLineSegment(sketch, "E15.30.6", {"start": v(62.77, -190) * mm, "end": v(68.4, -187.94) * mm});
            skLineSegment(sketch, "E15.30.9", {"start": v(74.04, -185.89) * mm, "end": v(68.4, -187.94) * mm});
            skPoint(sketch, "E15.30.15", {"position": v(79.87, -236.98) * mm});
            skLineSegment(sketch, "E15.30.16", {"start": v(91.14, -232.87) * mm, "end": v(91.1, -225.44) * mm});
            skLineSegment(sketch, "E15.30.17", {"start": v(79.87, -236.98) * mm, "end": v(75.12, -231.25) * mm});
            skLineSegment(sketch, "E15.30.18", {"start": v(79.87, -236.98) * mm, "end": v(85.5, -234.92) * mm, "construction": true});
            skLineSegment(sketch, "E15.30.19", {"start": v(91.1, -225.44) * mm, "end": v(88.75, -226.3) * mm});
            skLineSegment(sketch, "E15.31.0", {"start": v(117.56, -220.72) * mm, "end": v(112.2, -223.4) * mm, "construction": true});
            skLineSegment(sketch, "E15.31.1", {"start": v(101.46, -220.97) * mm, "end": v(103.7, -219.85) * mm});
            skLineSegment(sketch, "E15.31.4", {"start": v(103.7, -219.85) * mm, "end": v(84.4, -181.42) * mm});
            skLineSegment(sketch, "E15.31.5", {"start": v(114.42, -214.46) * mm, "end": v(95.12, -176.03) * mm});
            skLineSegment(sketch, "E15.31.6", {"start": v(84.4, -181.42) * mm, "end": v(89.76, -178.73) * mm});
            skLineSegment(sketch, "E15.31.9", {"start": v(95.12, -176.03) * mm, "end": v(89.76, -178.73) * mm});
            skPoint(sketch, "E15.31.15", {"position": v(106.84, -226.1) * mm});
            skLineSegment(sketch, "E15.31.16", {"start": v(117.56, -220.72) * mm, "end": v(116.65, -213.34) * mm});
            skLineSegment(sketch, "E15.31.17", {"start": v(106.84, -226.1) * mm, "end": v(101.46, -220.97) * mm});
            skLineSegment(sketch, "E15.31.18", {"start": v(106.84, -226.1) * mm, "end": v(112.2, -223.4) * mm, "construction": true});
            skLineSegment(sketch, "E15.31.19", {"start": v(116.65, -213.34) * mm, "end": v(114.42, -214.46) * mm});
            skLineSegment(sketch, "E15.32.0", {"start": v(142.4, -205.57) * mm, "end": v(137.38, -208.87) * mm, "construction": true});
            skLineSegment(sketch, "E15.32.1", {"start": v(126.43, -207.7) * mm, "end": v(128.52, -206.32) * mm});
            skLineSegment(sketch, "E15.32.4", {"start": v(128.52, -206.32) * mm, "end": v(104.89, -170.4) * mm});
            skLineSegment(sketch, "E15.32.5", {"start": v(138.54, -199.73) * mm, "end": v(114.91, -163.8) * mm});
            skLineSegment(sketch, "E15.32.6", {"start": v(104.89, -170.4) * mm, "end": v(109.9, -167.1) * mm});
            skLineSegment(sketch, "E15.32.9", {"start": v(114.91, -163.8) * mm, "end": v(109.9, -167.1) * mm});
            skPoint(sketch, "E15.32.15", {"position": v(132.36, -212.17) * mm});
            skLineSegment(sketch, "E15.32.16", {"start": v(142.4, -205.57) * mm, "end": v(140.63, -198.35) * mm});
            skLineSegment(sketch, "E15.32.17", {"start": v(132.36, -212.17) * mm, "end": v(126.43, -207.7) * mm});
            skLineSegment(sketch, "E15.32.18", {"start": v(132.36, -212.17) * mm, "end": v(137.38, -208.87) * mm, "construction": true});
            skLineSegment(sketch, "E15.32.19", {"start": v(140.63, -198.35) * mm, "end": v(138.54, -199.73) * mm});
            skLineSegment(sketch, "E15.33.0", {"start": v(165.3, -187.65) * mm, "end": v(160.7, -191.51) * mm, "construction": true});
            skLineSegment(sketch, "E15.33.1", {"start": v(149.69, -191.61) * mm, "end": v(151.6, -190) * mm});
            skLineSegment(sketch, "E15.33.4", {"start": v(151.6, -190) * mm, "end": v(123.96, -157.07) * mm});
            skLineSegment(sketch, "E15.33.5", {"start": v(160.8, -182.3) * mm, "end": v(133.15, -149.35) * mm});
            skLineSegment(sketch, "E15.33.6", {"start": v(123.96, -157.07) * mm, "end": v(128.56, -153.2) * mm});
            skLineSegment(sketch, "E15.33.9", {"start": v(133.15, -149.35) * mm, "end": v(128.56, -153.2) * mm});
            skPoint(sketch, "E15.33.15", {"position": v(156.1, -195.37) * mm});
            skLineSegment(sketch, "E15.33.16", {"start": v(165.3, -187.65) * mm, "end": v(162.7, -180.69) * mm});
            skLineSegment(sketch, "E15.33.17", {"start": v(156.1, -195.37) * mm, "end": v(149.69, -191.61) * mm});
            skLineSegment(sketch, "E15.33.18", {"start": v(156.1, -195.37) * mm, "end": v(160.7, -191.51) * mm, "construction": true});
            skLineSegment(sketch, "E15.33.19", {"start": v(162.7, -180.69) * mm, "end": v(160.8, -182.3) * mm});
            skLineSegment(sketch, "E15.34.0", {"start": v(185.96, -167.2) * mm, "end": v(181.84, -171.56) * mm, "construction": true});
            skLineSegment(sketch, "E15.34.1", {"start": v(170.92, -172.94) * mm, "end": v(172.63, -171.12) * mm});
            skLineSegment(sketch, "E15.34.4", {"start": v(172.63, -171.12) * mm, "end": v(141.36, -141.61) * mm});
            skLineSegment(sketch, "E15.34.5", {"start": v(180.87, -162.4) * mm, "end": v(149.6, -132.88) * mm});
            skLineSegment(sketch, "E15.34.6", {"start": v(141.36, -141.61) * mm, "end": v(145.47, -137.25) * mm});
            skLineSegment(sketch, "E15.34.9", {"start": v(149.6, -132.88) * mm, "end": v(145.47, -137.25) * mm});
            skPoint(sketch, "E15.34.15", {"position": v(177.73, -175.92) * mm});
            skLineSegment(sketch, "E15.34.16", {"start": v(185.96, -167.2) * mm, "end": v(182.58, -160.57) * mm});
            skLineSegment(sketch, "E15.34.17", {"start": v(177.73, -175.92) * mm, "end": v(170.92, -172.94) * mm});
            skLineSegment(sketch, "E15.34.18", {"start": v(177.73, -175.92) * mm, "end": v(181.84, -171.56) * mm, "construction": true});
            skLineSegment(sketch, "E15.34.19", {"start": v(182.58, -160.57) * mm, "end": v(180.87, -162.4) * mm});
            skLineSegment(sketch, "E15.35.0", {"start": v(204.11, -144.48) * mm, "end": v(200.53, -149.29) * mm, "construction": true});
            skLineSegment(sketch, "E15.35.1", {"start": v(189.84, -151.93) * mm, "end": v(191.33, -149.92) * mm});
            skLineSegment(sketch, "E15.35.4", {"start": v(191.33, -149.92) * mm, "end": v(156.84, -124.24) * mm});
            skLineSegment(sketch, "E15.35.5", {"start": v(198.5, -140.3) * mm, "end": v(164, -114.62) * mm});
            skLineSegment(sketch, "E15.35.6", {"start": v(156.84, -124.24) * mm, "end": v(160.42, -119.43) * mm});
            skLineSegment(sketch, "E15.35.9", {"start": v(164, -114.62) * mm, "end": v(160.42, -119.43) * mm});
            skPoint(sketch, "E15.35.15", {"position": v(196.95, -154.1) * mm});
            skLineSegment(sketch, "E15.35.16", {"start": v(204.11, -144.48) * mm, "end": v(200, -138.3) * mm});
            skLineSegment(sketch, "E15.35.17", {"start": v(196.95, -154.1) * mm, "end": v(189.84, -151.93) * mm});
            skLineSegment(sketch, "E15.35.18", {"start": v(196.95, -154.1) * mm, "end": v(200.53, -149.29) * mm, "construction": true});
            skLineSegment(sketch, "E15.35.19", {"start": v(200, -138.3) * mm, "end": v(198.5, -140.3) * mm});
            skLineSegment(sketch, "E15.36.0", {"start": v(219.5, -119.8) * mm, "end": v(216.5, -125) * mm, "construction": true});
            skLineSegment(sketch, "E15.36.1", {"start": v(206.2, -128.86) * mm, "end": v(207.44, -126.7) * mm});
            skLineSegment(sketch, "E15.36.4", {"start": v(207.44, -126.7) * mm, "end": v(170.2, -105.2) * mm});
            skLineSegment(sketch, "E15.36.5", {"start": v(213.44, -116.3) * mm, "end": v(176.2, -94.8) * mm});
            skLineSegment(sketch, "E15.36.6", {"start": v(170.2, -105.2) * mm, "end": v(173.2, -100) * mm});
            skLineSegment(sketch, "E15.36.9", {"start": v(176.2, -94.8) * mm, "end": v(173.2, -100) * mm});
            skPoint(sketch, "E15.36.15", {"position": v(213.5, -130.2) * mm});
            skLineSegment(sketch, "E15.36.16", {"start": v(219.5, -119.8) * mm, "end": v(214.7, -114.14) * mm});
            skLineSegment(sketch, "E15.36.17", {"start": v(213.5, -130.2) * mm, "end": v(206.2, -128.86) * mm});
            skLineSegment(sketch, "E15.36.18", {"start": v(213.5, -130.2) * mm, "end": v(216.5, -125) * mm, "construction": true});
            skLineSegment(sketch, "E15.36.19", {"start": v(214.7, -114.14) * mm, "end": v(213.44, -116.3) * mm});
            skLineSegment(sketch, "E15.37.0", {"start": v(231.93, -93.51) * mm, "end": v(229.55, -99.02) * mm, "construction": true});
            skLineSegment(sketch, "E15.37.1", {"start": v(219.76, -104.05) * mm, "end": v(220.75, -101.76) * mm});
            skLineSegment(sketch, "E15.37.4", {"start": v(220.75, -101.76) * mm, "end": v(181.27, -84.73) * mm});
            skLineSegment(sketch, "E15.37.5", {"start": v(225.5, -90.74) * mm, "end": v(186.02, -73.7) * mm});
            skLineSegment(sketch, "E15.37.6", {"start": v(181.27, -84.73) * mm, "end": v(183.64, -79.22) * mm});
            skLineSegment(sketch, "E15.37.9", {"start": v(186.02, -73.7) * mm, "end": v(183.64, -79.22) * mm});
            skPoint(sketch, "E15.37.15", {"position": v(227.18, -104.53) * mm});
            skLineSegment(sketch, "E15.37.16", {"start": v(231.93, -93.51) * mm, "end": v(226.5, -88.44) * mm});
            skLineSegment(sketch, "E15.37.17", {"start": v(227.18, -104.53) * mm, "end": v(219.76, -104.05) * mm});
            skLineSegment(sketch, "E15.37.18", {"start": v(227.18, -104.53) * mm, "end": v(229.55, -99.02) * mm, "construction": true});
            skLineSegment(sketch, "E15.37.19", {"start": v(226.5, -88.44) * mm, "end": v(225.5, -90.74) * mm});
            skLineSegment(sketch, "E15.38.0", {"start": v(241.22, -65.95) * mm, "end": v(239.5, -71.7) * mm, "construction": true});
            skLineSegment(sketch, "E15.38.1", {"start": v(230.35, -77.84) * mm, "end": v(231.07, -75.44) * mm});
            skLineSegment(sketch, "E15.38.4", {"start": v(231.07, -75.44) * mm, "end": v(189.88, -63.1) * mm});
            skLineSegment(sketch, "E15.38.5", {"start": v(234.51, -63.95) * mm, "end": v(193.32, -51.61) * mm});
            skLineSegment(sketch, "E15.38.6", {"start": v(189.88, -63.1) * mm, "end": v(191.6, -57.36) * mm});
            skLineSegment(sketch, "E15.38.9", {"start": v(193.32, -51.61) * mm, "end": v(191.6, -57.36) * mm});
            skPoint(sketch, "E15.38.15", {"position": v(237.78, -77.45) * mm});
            skLineSegment(sketch, "E15.38.16", {"start": v(241.22, -65.95) * mm, "end": v(235.23, -61.55) * mm});
            skLineSegment(sketch, "E15.38.17", {"start": v(237.78, -77.45) * mm, "end": v(230.35, -77.84) * mm});
            skLineSegment(sketch, "E15.38.18", {"start": v(237.78, -77.45) * mm, "end": v(239.5, -71.7) * mm, "construction": true});
            skLineSegment(sketch, "E15.38.19", {"start": v(235.23, -61.55) * mm, "end": v(234.51, -63.95) * mm});
            skLineSegment(sketch, "E15.39.0", {"start": v(247.24, -37.5) * mm, "end": v(246.2, -43.41) * mm, "construction": true});
            skLineSegment(sketch, "E15.39.1", {"start": v(237.83, -50.57) * mm, "end": v(238.27, -48.1) * mm});
            skLineSegment(sketch, "E15.39.4", {"start": v(238.27, -48.1) * mm, "end": v(195.92, -40.64) * mm});
            skLineSegment(sketch, "E15.39.5", {"start": v(240.35, -36.29) * mm, "end": v(198, -28.82) * mm});
            skLineSegment(sketch, "E15.39.6", {"start": v(195.92, -40.64) * mm, "end": v(196.96, -34.73) * mm});
            skLineSegment(sketch, "E15.39.9", {"start": v(198, -28.82) * mm, "end": v(196.96, -34.73) * mm});
            skPoint(sketch, "E15.39.15", {"position": v(245.16, -49.32) * mm});
            skLineSegment(sketch, "E15.39.16", {"start": v(247.24, -37.5) * mm, "end": v(240.78, -33.83) * mm});
            skLineSegment(sketch, "E15.39.17", {"start": v(245.16, -49.32) * mm, "end": v(237.83, -50.57) * mm});
            skLineSegment(sketch, "E15.39.18", {"start": v(245.16, -49.32) * mm, "end": v(246.2, -43.41) * mm, "construction": true});
            skLineSegment(sketch, "E15.39.19", {"start": v(240.78, -33.83) * mm, "end": v(240.35, -36.29) * mm});
            skLineSegment(sketch, "E15.40.0", {"start": v(249.93, -8.55) * mm, "end": v(249.58, -14.54) * mm, "construction": true});
            skLineSegment(sketch, "E15.40.1", {"start": v(242.1, -22.61) * mm, "end": v(242.24, -20.12) * mm});
            skLineSegment(sketch, "E15.40.4", {"start": v(242.24, -20.12) * mm, "end": v(199.31, -17.62) * mm});
            skLineSegment(sketch, "E15.40.5", {"start": v(242.94, -8.14) * mm, "end": v(200.01, -5.64) * mm});
            skLineSegment(sketch, "E15.40.6", {"start": v(199.31, -17.62) * mm, "end": v(199.66, -11.63) * mm});
            skLineSegment(sketch, "E15.40.9", {"start": v(200.01, -5.64) * mm, "end": v(199.66, -11.63) * mm});
            skPoint(sketch, "E15.40.15", {"position": v(249.23, -20.53) * mm});
            skLineSegment(sketch, "E15.40.16", {"start": v(249.93, -8.55) * mm, "end": v(243.08, -5.64) * mm});
            skLineSegment(sketch, "E15.40.17", {"start": v(249.23, -20.53) * mm, "end": v(242.1, -22.61) * mm});
            skLineSegment(sketch, "E15.40.18", {"start": v(249.23, -20.53) * mm, "end": v(249.58, -14.54) * mm, "construction": true});
            skLineSegment(sketch, "E15.40.19", {"start": v(243.08, -5.64) * mm, "end": v(242.94, -8.14) * mm});
            skLineSegment(sketch, "E15.41.0", {"start": v(249.23, 20.53) * mm, "end": v(249.58, 14.54) * mm, "construction": true});
            skLineSegment(sketch, "E15.41.1", {"start": v(243.08, 5.64) * mm, "end": v(242.94, 8.14) * mm});
            skLineSegment(sketch, "E15.41.4", {"start": v(242.94, 8.14) * mm, "end": v(200.01, 5.64) * mm});
            skLineSegment(sketch, "E15.41.5", {"start": v(242.24, 20.12) * mm, "end": v(199.31, 17.62) * mm});
            skLineSegment(sketch, "E15.41.6", {"start": v(200.01, 5.64) * mm, "end": v(199.66, 11.63) * mm});
            skLineSegment(sketch, "E15.41.9", {"start": v(199.31, 17.62) * mm, "end": v(199.66, 11.63) * mm});
            skPoint(sketch, "E15.41.15", {"position": v(249.93, 8.55) * mm});
            skLineSegment(sketch, "E15.41.16", {"start": v(249.23, 20.53) * mm, "end": v(242.1, 22.61) * mm});
            skLineSegment(sketch, "E15.41.17", {"start": v(249.93, 8.55) * mm, "end": v(243.08, 5.64) * mm});
            skLineSegment(sketch, "E15.41.18", {"start": v(249.93, 8.55) * mm, "end": v(249.58, 14.54) * mm, "construction": true});
            skLineSegment(sketch, "E15.41.19", {"start": v(242.1, 22.61) * mm, "end": v(242.24, 20.12) * mm});
            skLineSegment(sketch, "E15.42.0", {"start": v(245.16, 49.32) * mm, "end": v(246.2, 43.41) * mm, "construction": true});
            skLineSegment(sketch, "E15.42.1", {"start": v(240.78, 33.83) * mm, "end": v(240.35, 36.29) * mm});
            skLineSegment(sketch, "E15.42.4", {"start": v(240.35, 36.29) * mm, "end": v(198, 28.82) * mm});
            skLineSegment(sketch, "E15.42.5", {"start": v(238.27, 48.1) * mm, "end": v(195.92, 40.64) * mm});
            skLineSegment(sketch, "E15.42.6", {"start": v(198, 28.82) * mm, "end": v(196.96, 34.73) * mm});
            skLineSegment(sketch, "E15.42.9", {"start": v(195.92, 40.64) * mm, "end": v(196.96, 34.73) * mm});
            skPoint(sketch, "E15.42.15", {"position": v(247.24, 37.5) * mm});
            skLineSegment(sketch, "E15.42.16", {"start": v(245.16, 49.32) * mm, "end": v(237.83, 50.57) * mm});
            skLineSegment(sketch, "E15.42.17", {"start": v(247.24, 37.5) * mm, "end": v(240.78, 33.83) * mm});
            skLineSegment(sketch, "E15.42.18", {"start": v(247.24, 37.5) * mm, "end": v(246.2, 43.41) * mm, "construction": true});
            skLineSegment(sketch, "E15.42.19", {"start": v(237.83, 50.57) * mm, "end": v(238.27, 48.1) * mm});
            skLineSegment(sketch, "E15.43.0", {"start": v(237.78, 77.45) * mm, "end": v(239.5, 71.7) * mm, "construction": true});
            skLineSegment(sketch, "E15.43.1", {"start": v(235.23, 61.55) * mm, "end": v(234.51, 63.95) * mm});
            skLineSegment(sketch, "E15.43.4", {"start": v(234.51, 63.95) * mm, "end": v(193.32, 51.61) * mm});
            skLineSegment(sketch, "E15.43.5", {"start": v(231.07, 75.44) * mm, "end": v(189.88, 63.1) * mm});
            skLineSegment(sketch, "E15.43.6", {"start": v(193.32, 51.61) * mm, "end": v(191.6, 57.36) * mm});
            skLineSegment(sketch, "E15.43.9", {"start": v(189.88, 63.1) * mm, "end": v(191.6, 57.36) * mm});
            skPoint(sketch, "E15.43.15", {"position": v(241.22, 65.95) * mm});
            skLineSegment(sketch, "E15.43.16", {"start": v(237.78, 77.45) * mm, "end": v(230.35, 77.84) * mm});
            skLineSegment(sketch, "E15.43.17", {"start": v(241.22, 65.95) * mm, "end": v(235.23, 61.55) * mm});
            skLineSegment(sketch, "E15.43.18", {"start": v(241.22, 65.95) * mm, "end": v(239.5, 71.7) * mm, "construction": true});
            skLineSegment(sketch, "E15.43.19", {"start": v(230.35, 77.84) * mm, "end": v(231.07, 75.44) * mm});
            skLineSegment(sketch, "E15.44.0", {"start": v(227.18, 104.53) * mm, "end": v(229.55, 99.02) * mm, "construction": true});
            skLineSegment(sketch, "E15.44.1", {"start": v(226.5, 88.44) * mm, "end": v(225.5, 90.74) * mm});
            skLineSegment(sketch, "E15.44.4", {"start": v(225.5, 90.74) * mm, "end": v(186.02, 73.7) * mm});
            skLineSegment(sketch, "E15.44.5", {"start": v(220.75, 101.76) * mm, "end": v(181.27, 84.73) * mm});
            skLineSegment(sketch, "E15.44.6", {"start": v(186.02, 73.7) * mm, "end": v(183.64, 79.22) * mm});
            skLineSegment(sketch, "E15.44.9", {"start": v(181.27, 84.73) * mm, "end": v(183.64, 79.22) * mm});
            skPoint(sketch, "E15.44.15", {"position": v(231.93, 93.51) * mm});
            skLineSegment(sketch, "E15.44.16", {"start": v(227.18, 104.53) * mm, "end": v(219.76, 104.05) * mm});
            skLineSegment(sketch, "E15.44.17", {"start": v(231.93, 93.51) * mm, "end": v(226.5, 88.44) * mm});
            skLineSegment(sketch, "E15.44.18", {"start": v(231.93, 93.51) * mm, "end": v(229.55, 99.02) * mm, "construction": true});
            skLineSegment(sketch, "E15.44.19", {"start": v(219.76, 104.05) * mm, "end": v(220.75, 101.76) * mm});
            skLineSegment(sketch, "E15.45.0", {"start": v(213.5, 130.2) * mm, "end": v(216.5, 125) * mm, "construction": true});
            skLineSegment(sketch, "E15.45.1", {"start": v(214.7, 114.14) * mm, "end": v(213.44, 116.3) * mm});
            skLineSegment(sketch, "E15.45.4", {"start": v(213.44, 116.3) * mm, "end": v(176.2, 94.8) * mm});
            skLineSegment(sketch, "E15.45.5", {"start": v(207.44, 126.7) * mm, "end": v(170.2, 105.2) * mm});
            skLineSegment(sketch, "E15.45.6", {"start": v(176.2, 94.8) * mm, "end": v(173.2, 100) * mm});
            skLineSegment(sketch, "E15.45.9", {"start": v(170.2, 105.2) * mm, "end": v(173.2, 100) * mm});
            skPoint(sketch, "E15.45.15", {"position": v(219.5, 119.8) * mm});
            skLineSegment(sketch, "E15.45.16", {"start": v(213.5, 130.2) * mm, "end": v(206.2, 128.86) * mm});
            skLineSegment(sketch, "E15.45.17", {"start": v(219.5, 119.8) * mm, "end": v(214.7, 114.14) * mm});
            skLineSegment(sketch, "E15.45.18", {"start": v(219.5, 119.8) * mm, "end": v(216.5, 125) * mm, "construction": true});
            skLineSegment(sketch, "E15.45.19", {"start": v(206.2, 128.86) * mm, "end": v(207.44, 126.7) * mm});
            skLineSegment(sketch, "E15.46.0", {"start": v(196.95, 154.1) * mm, "end": v(200.53, 149.29) * mm, "construction": true});
            skLineSegment(sketch, "E15.46.1", {"start": v(200, 138.3) * mm, "end": v(198.5, 140.3) * mm});
            skLineSegment(sketch, "E15.46.4", {"start": v(198.5, 140.3) * mm, "end": v(164, 114.62) * mm});
            skLineSegment(sketch, "E15.46.5", {"start": v(191.33, 149.92) * mm, "end": v(156.84, 124.24) * mm});
            skLineSegment(sketch, "E15.46.6", {"start": v(164, 114.62) * mm, "end": v(160.42, 119.43) * mm});
            skLineSegment(sketch, "E15.46.9", {"start": v(156.84, 124.24) * mm, "end": v(160.42, 119.43) * mm});
            skPoint(sketch, "E15.46.15", {"position": v(204.11, 144.48) * mm});
            skLineSegment(sketch, "E15.46.16", {"start": v(196.95, 154.1) * mm, "end": v(189.84, 151.93) * mm});
            skLineSegment(sketch, "E15.46.17", {"start": v(204.11, 144.48) * mm, "end": v(200, 138.3) * mm});
            skLineSegment(sketch, "E15.46.18", {"start": v(204.11, 144.48) * mm, "end": v(200.53, 149.29) * mm, "construction": true});
            skLineSegment(sketch, "E15.46.19", {"start": v(189.84, 151.93) * mm, "end": v(191.33, 149.92) * mm});
            skLineSegment(sketch, "E15.47.0", {"start": v(177.73, 175.92) * mm, "end": v(181.84, 171.56) * mm, "construction": true});
            skLineSegment(sketch, "E15.47.1", {"start": v(182.58, 160.57) * mm, "end": v(180.87, 162.4) * mm});
            skLineSegment(sketch, "E15.47.4", {"start": v(180.87, 162.4) * mm, "end": v(149.6, 132.88) * mm});
            skLineSegment(sketch, "E15.47.5", {"start": v(172.63, 171.12) * mm, "end": v(141.36, 141.61) * mm});
            skLineSegment(sketch, "E15.47.6", {"start": v(149.6, 132.88) * mm, "end": v(145.47, 137.25) * mm});
            skLineSegment(sketch, "E15.47.9", {"start": v(141.36, 141.61) * mm, "end": v(145.47, 137.25) * mm});
            skPoint(sketch, "E15.47.15", {"position": v(185.96, 167.2) * mm});
            skLineSegment(sketch, "E15.47.16", {"start": v(177.73, 175.92) * mm, "end": v(170.92, 172.94) * mm});
            skLineSegment(sketch, "E15.47.17", {"start": v(185.96, 167.2) * mm, "end": v(182.58, 160.57) * mm});
            skLineSegment(sketch, "E15.47.18", {"start": v(185.96, 167.2) * mm, "end": v(181.84, 171.56) * mm, "construction": true});
            skLineSegment(sketch, "E15.47.19", {"start": v(170.92, 172.94) * mm, "end": v(172.63, 171.12) * mm});
            skLineSegment(sketch, "E15.48.0", {"start": v(156.1, 195.37) * mm, "end": v(160.7, 191.51) * mm, "construction": true});
            skLineSegment(sketch, "E15.48.1", {"start": v(162.7, 180.69) * mm, "end": v(160.8, 182.3) * mm});
            skLineSegment(sketch, "E15.48.4", {"start": v(160.8, 182.3) * mm, "end": v(133.15, 149.35) * mm});
            skLineSegment(sketch, "E15.48.5", {"start": v(151.6, 190) * mm, "end": v(123.96, 157.07) * mm});
            skLineSegment(sketch, "E15.48.6", {"start": v(133.15, 149.35) * mm, "end": v(128.56, 153.2) * mm});
            skLineSegment(sketch, "E15.48.9", {"start": v(123.96, 157.07) * mm, "end": v(128.56, 153.2) * mm});
            skPoint(sketch, "E15.48.15", {"position": v(165.3, 187.65) * mm});
            skLineSegment(sketch, "E15.48.16", {"start": v(156.1, 195.37) * mm, "end": v(149.69, 191.61) * mm});
            skLineSegment(sketch, "E15.48.17", {"start": v(165.3, 187.65) * mm, "end": v(162.7, 180.69) * mm});
            skLineSegment(sketch, "E15.48.18", {"start": v(165.3, 187.65) * mm, "end": v(160.7, 191.51) * mm, "construction": true});
            skLineSegment(sketch, "E15.48.19", {"start": v(149.69, 191.61) * mm, "end": v(151.6, 190) * mm});
            skLineSegment(sketch, "E15.49.0", {"start": v(132.36, 212.17) * mm, "end": v(137.38, 208.87) * mm, "construction": true});
            skLineSegment(sketch, "E15.49.1", {"start": v(140.63, 198.35) * mm, "end": v(138.54, 199.73) * mm});
            skLineSegment(sketch, "E15.49.4", {"start": v(138.54, 199.73) * mm, "end": v(114.91, 163.8) * mm});
            skLineSegment(sketch, "E15.49.5", {"start": v(128.52, 206.32) * mm, "end": v(104.89, 170.4) * mm});
            skLineSegment(sketch, "E15.49.6", {"start": v(114.91, 163.8) * mm, "end": v(109.9, 167.1) * mm});
            skLineSegment(sketch, "E15.49.9", {"start": v(104.89, 170.4) * mm, "end": v(109.9, 167.1) * mm});
            skPoint(sketch, "E15.49.15", {"position": v(142.4, 205.57) * mm});
            skLineSegment(sketch, "E15.49.16", {"start": v(132.36, 212.17) * mm, "end": v(126.43, 207.7) * mm});
            skLineSegment(sketch, "E15.49.17", {"start": v(142.4, 205.57) * mm, "end": v(140.63, 198.35) * mm});
            skLineSegment(sketch, "E15.49.18", {"start": v(142.4, 205.57) * mm, "end": v(137.38, 208.87) * mm, "construction": true});
            skLineSegment(sketch, "E15.49.19", {"start": v(126.43, 207.7) * mm, "end": v(128.52, 206.32) * mm});
            skLineSegment(sketch, "E15.50.0", {"start": v(106.84, 226.1) * mm, "end": v(112.2, 223.4) * mm, "construction": true});
            skLineSegment(sketch, "E15.50.1", {"start": v(116.65, 213.34) * mm, "end": v(114.42, 214.46) * mm});
            skLineSegment(sketch, "E15.50.4", {"start": v(114.42, 214.46) * mm, "end": v(95.12, 176.03) * mm});
            skLineSegment(sketch, "E15.50.5", {"start": v(103.7, 219.85) * mm, "end": v(84.4, 181.42) * mm});
            skLineSegment(sketch, "E15.50.6", {"start": v(95.12, 176.03) * mm, "end": v(89.76, 178.73) * mm});
            skLineSegment(sketch, "E15.50.9", {"start": v(84.4, 181.42) * mm, "end": v(89.76, 178.73) * mm});
            skPoint(sketch, "E15.50.15", {"position": v(117.56, 220.72) * mm});
            skLineSegment(sketch, "E15.50.16", {"start": v(106.84, 226.1) * mm, "end": v(101.46, 220.97) * mm});
            skLineSegment(sketch, "E15.50.17", {"start": v(117.56, 220.72) * mm, "end": v(116.65, 213.34) * mm});
            skLineSegment(sketch, "E15.50.18", {"start": v(117.56, 220.72) * mm, "end": v(112.2, 223.4) * mm, "construction": true});
            skLineSegment(sketch, "E15.50.19", {"start": v(101.46, 220.97) * mm, "end": v(103.7, 219.85) * mm});
            skLineSegment(sketch, "E15.51.0", {"start": v(79.87, 236.98) * mm, "end": v(85.5, 234.92) * mm, "construction": true});
            skLineSegment(sketch, "E15.51.1", {"start": v(91.1, 225.44) * mm, "end": v(88.75, 226.3) * mm});
            skLineSegment(sketch, "E15.51.4", {"start": v(88.75, 226.3) * mm, "end": v(74.04, 185.89) * mm});
            skLineSegment(sketch, "E15.51.5", {"start": v(77.47, 230.4) * mm, "end": v(62.77, 190) * mm});
            skLineSegment(sketch, "E15.51.6", {"start": v(74.04, 185.89) * mm, "end": v(68.4, 187.94) * mm});
            skLineSegment(sketch, "E15.51.9", {"start": v(62.77, 190) * mm, "end": v(68.4, 187.94) * mm});
            skPoint(sketch, "E15.51.15", {"position": v(91.14, 232.87) * mm});
            skLineSegment(sketch, "E15.51.16", {"start": v(79.87, 236.98) * mm, "end": v(75.12, 231.25) * mm});
            skLineSegment(sketch, "E15.51.17", {"start": v(91.14, 232.87) * mm, "end": v(91.1, 225.44) * mm});
            skLineSegment(sketch, "E15.51.18", {"start": v(91.14, 232.87) * mm, "end": v(85.5, 234.92) * mm, "construction": true});
            skLineSegment(sketch, "E15.51.19", {"start": v(75.12, 231.25) * mm, "end": v(77.47, 230.4) * mm});
            skLineSegment(sketch, "E15.52.0", {"start": v(51.82, 244.64) * mm, "end": v(57.65, 243.26) * mm, "construction": true});
            skLineSegment(sketch, "E15.52.1", {"start": v(64.31, 234.49) * mm, "end": v(61.88, 235.07) * mm});
            skLineSegment(sketch, "E15.52.4", {"start": v(61.88, 235.07) * mm, "end": v(51.96, 193.23) * mm});
            skLineSegment(sketch, "E15.52.5", {"start": v(50.2, 237.83) * mm, "end": v(40.28, 196) * mm});
            skLineSegment(sketch, "E15.52.6", {"start": v(51.96, 193.23) * mm, "end": v(46.12, 194.6) * mm});
            skLineSegment(sketch, "E15.52.9", {"start": v(40.28, 196) * mm, "end": v(46.12, 194.6) * mm});
            skPoint(sketch, "E15.52.15", {"position": v(63.5, 241.88) * mm});
            skLineSegment(sketch, "E15.52.16", {"start": v(51.82, 244.64) * mm, "end": v(47.77, 238.41) * mm});
            skLineSegment(sketch, "E15.52.17", {"start": v(63.5, 241.88) * mm, "end": v(64.31, 234.49) * mm});
            skLineSegment(sketch, "E15.52.18", {"start": v(63.5, 241.88) * mm, "end": v(57.65, 243.26) * mm, "construction": true});
            skLineSegment(sketch, "E15.52.19", {"start": v(47.77, 238.41) * mm, "end": v(50.2, 237.83) * mm});
            skLineSegment(sketch, "E15.53.0", {"start": v(23.06, 249) * mm, "end": v(29.02, 248.3) * mm, "construction": true});
            skLineSegment(sketch, "E15.53.1", {"start": v(36.65, 240.37) * mm, "end": v(34.17, 240.66) * mm});
            skLineSegment(sketch, "E15.53.4", {"start": v(34.17, 240.66) * mm, "end": v(29.18, 197.95) * mm});
            skLineSegment(sketch, "E15.53.5", {"start": v(22.25, 242.05) * mm, "end": v(17.26, 199.34) * mm});
            skLineSegment(sketch, "E15.53.6", {"start": v(29.18, 197.95) * mm, "end": v(23.22, 198.65) * mm});
            skLineSegment(sketch, "E15.53.9", {"start": v(17.26, 199.34) * mm, "end": v(23.22, 198.65) * mm});
            skPoint(sketch, "E15.53.15", {"position": v(34.98, 247.61) * mm});
            skLineSegment(sketch, "E15.53.16", {"start": v(23.06, 249) * mm, "end": v(19.77, 242.34) * mm});
            skLineSegment(sketch, "E15.53.17", {"start": v(34.98, 247.61) * mm, "end": v(36.65, 240.37) * mm});
            skLineSegment(sketch, "E15.53.18", {"start": v(34.98, 247.61) * mm, "end": v(29.02, 248.3) * mm, "construction": true});
            skLineSegment(sketch, "E15.53.19", {"start": v(19.77, 242.34) * mm, "end": v(22.25, 242.05) * mm});
            skLineSegment(sketch, "E16", {"start": v(-23.06, 249) * mm, "end": v(-6, 250) * mm});
            skLineSegment(sketch, "E17.1.0", {"start": v(-51.82, 244.64) * mm, "end": v(-34.98, 247.61) * mm});
            skLineSegment(sketch, "E17.2.0", {"start": v(-79.87, 236.98) * mm, "end": v(-63.5, 241.88) * mm});
            skLineSegment(sketch, "E17.3.0", {"start": v(-106.84, 226.1) * mm, "end": v(-91.14, 232.87) * mm});
            skLineSegment(sketch, "E17.4.0", {"start": v(-132.36, 212.17) * mm, "end": v(-117.56, 220.72) * mm});
            skLineSegment(sketch, "E17.5.0", {"start": v(-156.1, 195.37) * mm, "end": v(-142.4, 205.57) * mm});
            skLineSegment(sketch, "E17.6.0", {"start": v(-177.73, 175.92) * mm, "end": v(-165.3, 187.65) * mm});
            skLineSegment(sketch, "E17.7.0", {"start": v(-196.95, 154.1) * mm, "end": v(-185.96, 167.2) * mm});
            skLineSegment(sketch, "E17.8.0", {"start": v(-213.5, 130.2) * mm, "end": v(-204.11, 144.48) * mm});
            skLineSegment(sketch, "E17.9.0", {"start": v(-227.18, 104.53) * mm, "end": v(-219.5, 119.8) * mm});
            skLineSegment(sketch, "E17.10.0", {"start": v(-237.78, 77.45) * mm, "end": v(-231.93, 93.51) * mm});
            skLineSegment(sketch, "E17.11.0", {"start": v(-245.16, 49.32) * mm, "end": v(-241.22, 65.95) * mm});
            skLineSegment(sketch, "E17.12.0", {"start": v(-249.23, 20.53) * mm, "end": v(-247.24, 37.5) * mm});
            skLineSegment(sketch, "E17.13.0", {"start": v(-249.93, -8.55) * mm, "end": v(-249.93, 8.55) * mm});
            skLineSegment(sketch, "E17.14.0", {"start": v(-247.24, -37.5) * mm, "end": v(-249.23, -20.53) * mm});
            skLineSegment(sketch, "E17.15.0", {"start": v(-241.22, -65.95) * mm, "end": v(-245.16, -49.32) * mm});
            skLineSegment(sketch, "E17.16.0", {"start": v(-231.93, -93.51) * mm, "end": v(-237.78, -77.45) * mm});
            skLineSegment(sketch, "E17.17.0", {"start": v(-219.5, -119.8) * mm, "end": v(-227.18, -104.53) * mm});
            skLineSegment(sketch, "E17.18.0", {"start": v(-204.11, -144.48) * mm, "end": v(-213.5, -130.2) * mm});
            skLineSegment(sketch, "E17.19.0", {"start": v(-185.96, -167.2) * mm, "end": v(-196.95, -154.1) * mm});
            skLineSegment(sketch, "E17.20.0", {"start": v(-165.3, -187.65) * mm, "end": v(-177.73, -175.92) * mm});
            skLineSegment(sketch, "E17.21.0", {"start": v(-142.4, -205.57) * mm, "end": v(-156.1, -195.37) * mm});
            skLineSegment(sketch, "E17.22.0", {"start": v(-117.56, -220.72) * mm, "end": v(-132.36, -212.17) * mm});
            skLineSegment(sketch, "E17.23.0", {"start": v(-91.14, -232.87) * mm, "end": v(-106.84, -226.1) * mm});
            skLineSegment(sketch, "E17.24.0", {"start": v(-63.5, -241.88) * mm, "end": v(-79.87, -236.98) * mm});
            skLineSegment(sketch, "E17.25.0", {"start": v(-34.98, -247.61) * mm, "end": v(-51.82, -244.64) * mm});
            skLineSegment(sketch, "E17.26.0", {"start": v(-6, -250) * mm, "end": v(-23.06, -249) * mm});
            skLineSegment(sketch, "E17.27.0", {"start": v(23.06, -249) * mm, "end": v(6, -250) * mm});
            skLineSegment(sketch, "E17.28.0", {"start": v(51.82, -244.64) * mm, "end": v(34.98, -247.61) * mm});
            skLineSegment(sketch, "E17.29.0", {"start": v(79.87, -236.98) * mm, "end": v(63.5, -241.88) * mm});
            skLineSegment(sketch, "E17.30.0", {"start": v(106.84, -226.1) * mm, "end": v(91.14, -232.87) * mm});
            skLineSegment(sketch, "E17.31.0", {"start": v(132.36, -212.17) * mm, "end": v(117.56, -220.72) * mm});
            skLineSegment(sketch, "E17.32.0", {"start": v(156.1, -195.37) * mm, "end": v(142.4, -205.57) * mm});
            skLineSegment(sketch, "E17.33.0", {"start": v(177.73, -175.92) * mm, "end": v(165.3, -187.65) * mm});
            skLineSegment(sketch, "E17.34.0", {"start": v(196.95, -154.1) * mm, "end": v(185.96, -167.2) * mm});
            skLineSegment(sketch, "E17.35.0", {"start": v(213.5, -130.2) * mm, "end": v(204.11, -144.48) * mm});
            skLineSegment(sketch, "E17.36.0", {"start": v(227.18, -104.53) * mm, "end": v(219.5, -119.8) * mm});
            skLineSegment(sketch, "E17.37.0", {"start": v(237.78, -77.45) * mm, "end": v(231.93, -93.51) * mm});
            skLineSegment(sketch, "E17.38.0", {"start": v(245.16, -49.32) * mm, "end": v(241.22, -65.95) * mm});
            skLineSegment(sketch, "E17.39.0", {"start": v(249.23, -20.53) * mm, "end": v(247.24, -37.5) * mm});
            skLineSegment(sketch, "E17.40.0", {"start": v(249.93, 8.55) * mm, "end": v(249.93, -8.55) * mm});
            skLineSegment(sketch, "E17.41.0", {"start": v(247.24, 37.5) * mm, "end": v(249.23, 20.53) * mm});
            skLineSegment(sketch, "E17.42.0", {"start": v(241.22, 65.95) * mm, "end": v(245.16, 49.32) * mm});
            skLineSegment(sketch, "E17.43.0", {"start": v(231.93, 93.51) * mm, "end": v(237.78, 77.45) * mm});
            skLineSegment(sketch, "E17.44.0", {"start": v(219.5, 119.8) * mm, "end": v(227.18, 104.53) * mm});
            skLineSegment(sketch, "E17.45.0", {"start": v(204.11, 144.48) * mm, "end": v(213.5, 130.2) * mm});
            skLineSegment(sketch, "E17.46.0", {"start": v(185.96, 167.2) * mm, "end": v(196.95, 154.1) * mm});
            skLineSegment(sketch, "E17.47.0", {"start": v(165.3, 187.65) * mm, "end": v(177.73, 175.92) * mm});
            skLineSegment(sketch, "E17.48.0", {"start": v(142.4, 205.57) * mm, "end": v(156.1, 195.37) * mm});
            skLineSegment(sketch, "E17.49.0", {"start": v(117.56, 220.72) * mm, "end": v(132.36, 212.17) * mm});
            skLineSegment(sketch, "E17.50.0", {"start": v(91.14, 232.87) * mm, "end": v(106.84, 226.1) * mm});
            skLineSegment(sketch, "E17.51.0", {"start": v(63.5, 241.88) * mm, "end": v(79.87, 236.98) * mm});
            skLineSegment(sketch, "E17.52.0", {"start": v(34.98, 247.61) * mm, "end": v(51.82, 244.64) * mm});
            skLineSegment(sketch, "E17.53.0", {"start": v(6, 250) * mm, "end": v(23.06, 249) * mm});
            skSolve(sketch);
        }
        {
            var Q0;
            Q0=qSketchRegion(id+"F0",true);
            var Q1;
            Q1=makeQuery(id+"F0.imprint","IMPRINT",FACE,{"disambiguationData":[TD([[makeQuery(id+"F0.imprint","IMPRINT",EDGE,{"derivedFrom":sQuery(id+"F0.wireOp",EDGE,"E1")}),-1.0]])]});
            extrude(context, id + "F1", {"entities" : qUnion([Q0, Q1]), "depth" : 500 * mm});
        }
    });
